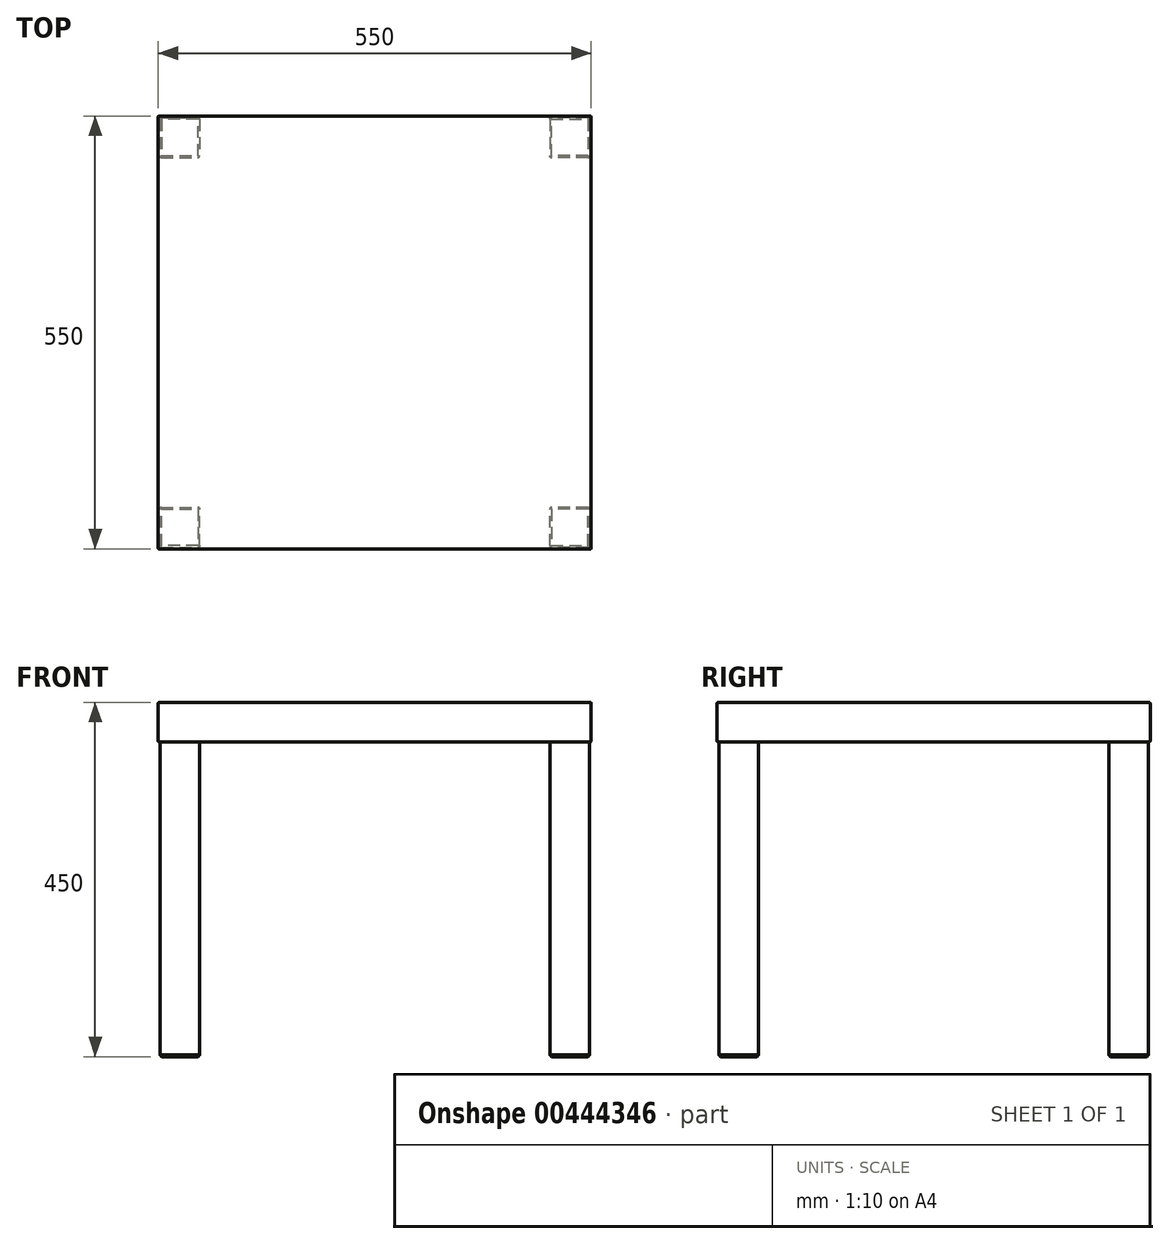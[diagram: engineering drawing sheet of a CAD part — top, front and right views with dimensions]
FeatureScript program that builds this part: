
annotation { "Feature Type Name" : "Feature", "Feature Type Description" : "" }
export const myFeature = defineFeature(function(context is Context, id is Id, definition is map)
    precondition{}
    {
        {
            var Q0;
            Q0=qCreatedBy(makeId("Top.planeOp"),FACE);
            var sketch = newSketch(context, id + "F0", { "sketchPlane" : qUnion([Q0])});
            skLineSegment(sketch, "E0.bottom", {"start": v(275, 275) * mm, "end": v(-275, 275) * mm, "construction": true});
            skLineSegment(sketch, "E0.top", {"start": v(275, -275) * mm, "end": v(-275, -275) * mm, "construction": true});
            skLineSegment(sketch, "E0.left", {"start": v(275, 275) * mm, "end": v(275, -275) * mm, "construction": true});
            skLineSegment(sketch, "E0.right", {"start": v(-275, 275) * mm, "end": v(-275, -275) * mm, "construction": true});
            skPoint(sketch, "E0.middle", {"position": v(0, 0) * mm});
            skLineSegment(sketch, "E1.bottom", {"start": v(-272.9, -272.9) * mm, "end": v(-222.4, -272.9) * mm});
            skLineSegment(sketch, "E1.top", {"start": v(-272.9, -222.4) * mm, "end": v(-222.4, -222.4) * mm});
            skLineSegment(sketch, "E1.left", {"start": v(-272.9, -272.9) * mm, "end": v(-272.9, -222.4) * mm});
            skLineSegment(sketch, "E1.right", {"start": v(-222.4, -272.9) * mm, "end": v(-222.4, -222.4) * mm});
            skLineSegment(sketch, "E2.bottom", {"start": v(-275, -275) * mm, "end": v(0, -275) * mm});
            skLineSegment(sketch, "E2.top", {"start": v(-275, 0) * mm, "end": v(0, 0) * mm});
            skLineSegment(sketch, "E2.left", {"start": v(-275, -275) * mm, "end": v(-275, 0) * mm});
            skLineSegment(sketch, "E2.right", {"start": v(0, -275) * mm, "end": v(0, 0) * mm});
            skSolve(sketch);
        }
        {
            var Q0;
            Q0=makeQuery(id+"F0.imprint","IMPRINT",FACE,{"disambiguationData":[TD([[makeQuery(id+"F0.imprint","IMPRINT",EDGE,{"derivedFrom":sQuery(id+"F0.wireOp",EDGE,"E1.bottom")}),-1.0]])]});
            var Q1;
            Q1=makeQuery(id+"F0.imprint","IMPRINT",FACE,{"disambiguationData":[TD([[makeQuery(id+"F0.imprint","IMPRINT",EDGE,{"derivedFrom":sQuery(id+"F0.wireOp",EDGE,"E1.bottom")}),1.0]])]});
            extrude(context, id + "F1", {"entities" : qUnion([Q0, Q1]), "depth" : 50 * mm, "offsetDistance" : 25 * mm});
        }
        {
            var Q0;
            Q0=makeQuery(id+"F0.imprint","IMPRINT",FACE,{"disambiguationData":[TD([[makeQuery(id+"F0.imprint","IMPRINT",EDGE,{"derivedFrom":sQuery(id+"F0.wireOp",EDGE,"E1.bottom")}),1.0]])]});
            extrude(context, id + "F2", {"entities" : qUnion([Q0]), "operationType" : NewBodyOperationType.ADD, "oppositeDirection" : true, "depth" : 400 * mm, "offsetDistance" : 25 * mm});
        }
        {
            var Q0;
            Q0=makeQuery(id+"F2.opExtrude","CAP_FACE",FACE,{"disambiguationData":[OSD([sQuery(id+"F0.wireOp",EDGE,"E1.bottom"),sQuery(id+"F0.wireOp",EDGE,"E1.top"),sQuery(id+"F0.wireOp",EDGE,"E1.left"),sQuery(id+"F0.wireOp",EDGE,"E1.right")])],"isStart":false});
            chamfer(context, id + "F3", {"entities" : qUnion([Q0]), "width" : 2 * mm, "tangentPropagation" : true});
        }
        {
            var Q0;
            Q0=makeQuery(id+"F2.opExtrude","SWEPT_EDGE",EDGE,{"disambiguationData":[OSD([sQuery(id+"F0.wireOp",EDGE,"E1.bottom"),sQuery(id+"F0.wireOp",EDGE,"E1.left")])]});
            var Q1;
            Q1=makeQuery(id+"F2.opExtrude","SWEPT_EDGE",EDGE,{"disambiguationData":[OSD([sQuery(id+"F0.wireOp",EDGE,"E1.bottom"),sQuery(id+"F0.wireOp",EDGE,"E1.right")])]});
            var Q2;
            Q2=makeQuery(id+"F2.opExtrude","SWEPT_EDGE",EDGE,{"disambiguationData":[OSD([sQuery(id+"F0.wireOp",EDGE,"E1.top"),sQuery(id+"F0.wireOp",EDGE,"E1.left")])]});
            var Q3;
            Q3=makeQuery(id+"F2.opExtrude","SWEPT_EDGE",EDGE,{"disambiguationData":[OSD([sQuery(id+"F0.wireOp",EDGE,"E1.top"),sQuery(id+"F0.wireOp",EDGE,"E1.right")])]});
            fillet(context, id + "F4", {"entities" : qUnion([Q0, Q1, Q2, Q3]), "radius" : 2 * mm, "tangentPropagation" : true, "allowEdgeOverflow" : false});
        }
        {
            var Q0;
            Q0=makeQuery(id+"F1.opExtrude","CAP_EDGE",EDGE,{"disambiguationData":[OSD([sQuery(id+"F0.wireOp",EDGE,"E2.left")])],"isStart":false});
            var Q1;
            Q1=makeQuery(id+"F1.opExtrude","CAP_EDGE",EDGE,{"disambiguationData":[OSD([sQuery(id+"F0.wireOp",EDGE,"E2.left")])],"isStart":true});
            var Q2;
            Q2=makeQuery(id+"F1.opExtrude","SWEPT_EDGE",EDGE,{"disambiguationData":[OSD([sQuery(id+"F0.wireOp",EDGE,"E2.bottom"),sQuery(id+"F0.wireOp",EDGE,"E2.left")])]});
            var Q3;
            Q3=makeQuery(id+"F1.opExtrude","CAP_EDGE",EDGE,{"disambiguationData":[OSD([sQuery(id+"F0.wireOp",EDGE,"E2.bottom")])],"isStart":false});
            var Q4;
            Q4=makeQuery(id+"F1.opExtrude","CAP_EDGE",EDGE,{"disambiguationData":[OSD([sQuery(id+"F0.wireOp",EDGE,"E2.bottom")])],"isStart":true});
            fillet(context, id + "F5", {"entities" : qUnion([Q0, Q1, Q2, Q3, Q4]), "radius" : 1 * mm, "tangentPropagation" : true, "allowEdgeOverflow" : false});
        }
        {
            var Q0;
            Q0=makeQuery(id+"F1.opExtrude","SWEPT_BODY",BODY,{"disambiguationData":[OSD([sQuery(id+"F0.wireOp",EDGE,"E2.bottom"),sQuery(id+"F0.wireOp",EDGE,"E2.top"),sQuery(id+"F0.wireOp",EDGE,"E2.left"),sQuery(id+"F0.wireOp",EDGE,"E2.right")])]});
            var Q1;
            Q1=makeQuery(id+"F1.opExtrude","SWEPT_FACE",FACE,{"disambiguationData":[OSD([sQuery(id+"F0.wireOp",EDGE,"E2.right")])]});
            mirror(context, id + "F6", {"operationType" : NewBodyOperationType.ADD, "entities" : qUnion([Q0]), "mirrorPlane" : qUnion([Q1])});
        }
        {
            var Q0;
            Q0=makeQuery(id+"F1.opExtrude","SWEPT_BODY",BODY,{"disambiguationData":[OSD([sQuery(id+"F0.wireOp",EDGE,"E2.bottom"),sQuery(id+"F0.wireOp",EDGE,"E2.top"),sQuery(id+"F0.wireOp",EDGE,"E2.left"),sQuery(id+"F0.wireOp",EDGE,"E2.right")])]});
            var Q1;
            {var subQ0=makeQuery(id+"F1.opExtrude","SWEPT_FACE",FACE,{"disambiguationData":[OSD([sQuery(id+"F0.wireOp",EDGE,"E2.top")])]});Q1=makeQuery(id+"F6.boolean.opBoolean","MERGE",FACE,{"derivedFrom":[subQ0,makeQuery(id+"F6.opPattern","COPY",FACE,{"derivedFrom":subQ0,"instanceName":"1"})]});}
            mirror(context, id + "F7", {"operationType" : NewBodyOperationType.ADD, "entities" : qUnion([Q0]), "mirrorPlane" : qUnion([Q1])});
        }
    });
